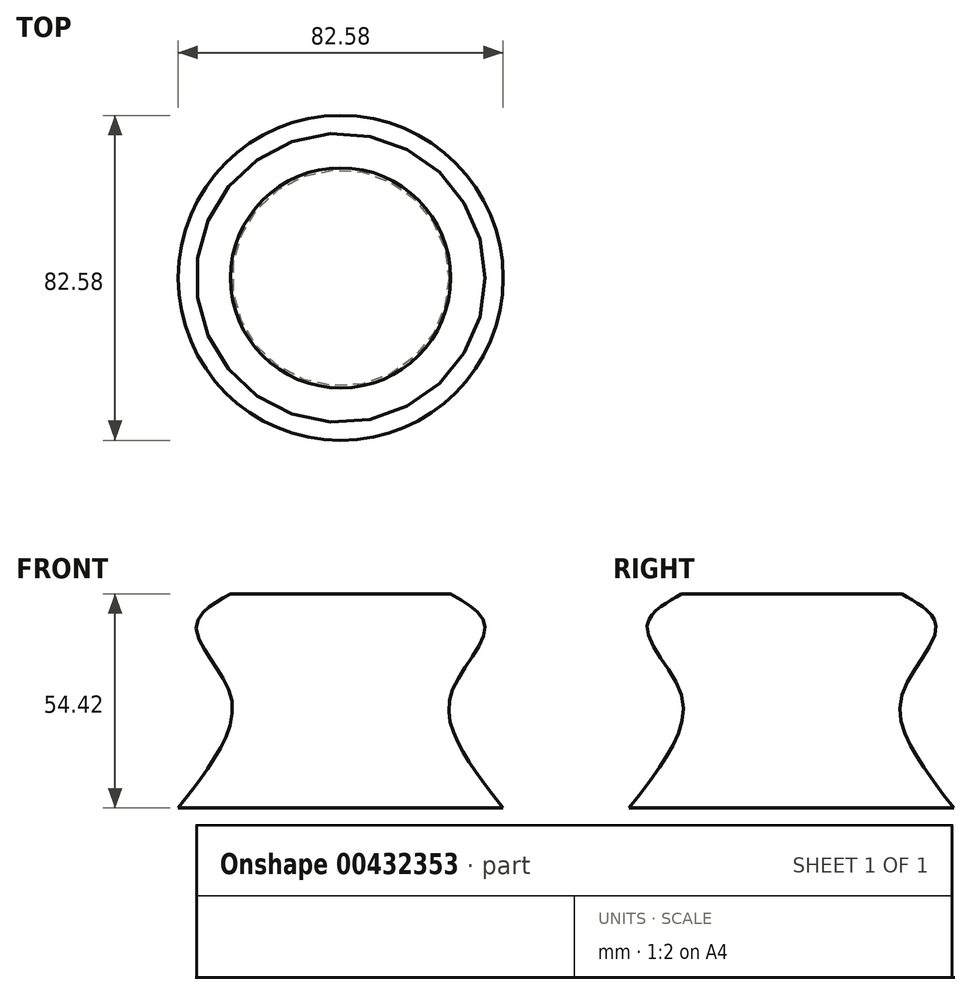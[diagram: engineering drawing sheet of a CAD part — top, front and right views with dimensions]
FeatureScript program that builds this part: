
annotation { "Feature Type Name" : "Feature", "Feature Type Description" : "" }
export const myFeature = defineFeature(function(context is Context, id is Id, definition is map)
    precondition{}
    {
        {
            var Q0;
            Q0=qCreatedBy(makeId("Front.planeOp"),FACE);
            var sketch = newSketch(context, id + "F0", { "sketchPlane" : qUnion([Q0])});
            skFitSpline(sketch, "E0", {"points": [v(-27.97, 44.05) * mm, v(-36.72, 35.49) * mm, v(-28.16, 18.93) * mm, v(-31.01, 4.1) * mm, v(-41.29, -10.37) * mm], "startDerivative": vector(-59.6, -33.67) * mm, "endDerivative": vector(-41.89, -53.4) * mm});
            skLineSegment(sketch, "E1", {"start": v(-41.29, -10.37) * mm, "end": v(0, -10.37) * mm});
            skLineSegment(sketch, "E2", {"start": v(-27.97, 44.05) * mm, "end": v(0, 44.05) * mm});
            skLineSegment(sketch, "E3", {"start": v(0, 44.05) * mm, "end": v(0, -10.37) * mm});
            skSolve(sketch);
        }
        {
            var Q0;
            Q0 = qSketchRegion(id + "F0", true);
            var Q1;
            Q1 = qSketchRegion(id + "F2", true);
            var Q2;
            Q2=sQuery(id+"F0.wireOp",EDGE,"E3");
            revolve(context, id + "F1", {"entities" : qUnion([Q0, Q1]), "axis" : qUnion([Q2]), "revolveType" : RevolveType.ONE_DIRECTION, "angle" : 360 * degree});
        }
        {
            var Q0;
            Q0=makeQuery(id+"F1.opRevolve","SWEPT_FACE",FACE,{"disambiguationData":[OSD([sQuery(id+"F0.wireOp",EDGE,"E1")])]});
            var sketch = newSketch(context, id + "F2", { "sketchPlane" : qUnion([Q0])});
            skCircle(sketch, "E4", {"center": v(1.52, 0) * mm, "radius": 29.14 * mm});
            skSolve(sketch);
        }
        {
            var Q0;
            Q0=makeQuery(id+"F2.imprint","IMPRINT",FACE,{"disambiguationData":[TD([[makeQuery(id+"F2.imprint","IMPRINT",EDGE,{"derivedFrom":sQuery(id+"F2.wireOp",EDGE,"E4")}),1.0]])]});
            extrude(context, id + "F3", {"entities" : qUnion([Q0]), "operationType" : NewBodyOperationType.ADD, "oppositeDirection" : true, "depth" : 14.73 * mm});
        }
    });
